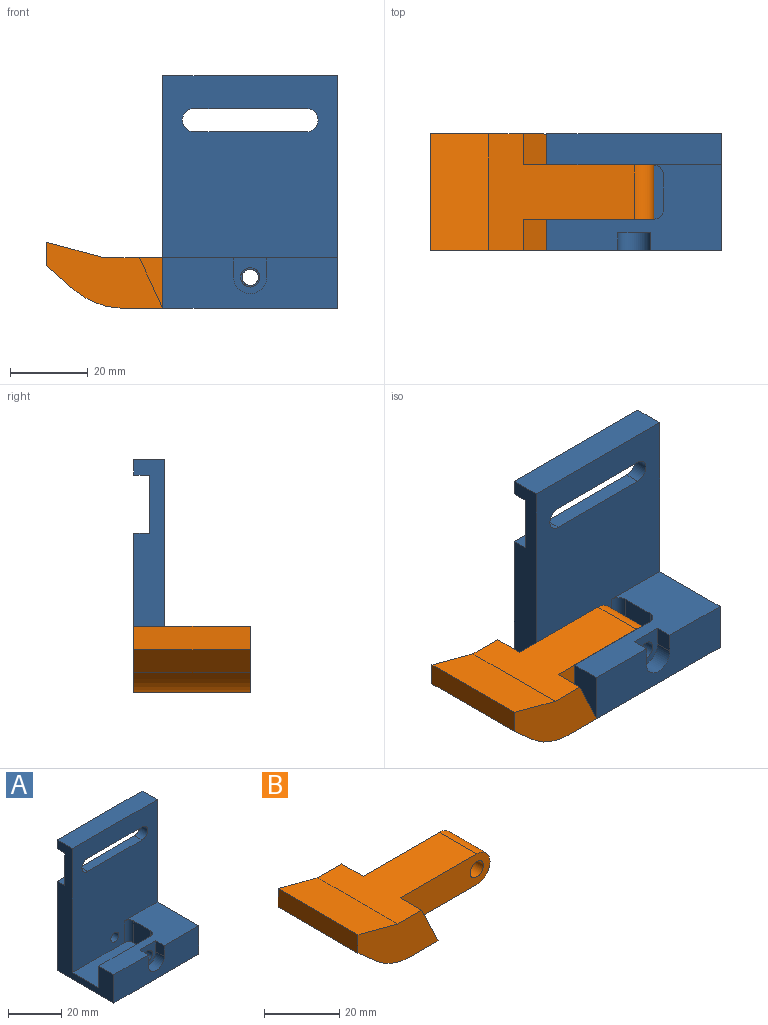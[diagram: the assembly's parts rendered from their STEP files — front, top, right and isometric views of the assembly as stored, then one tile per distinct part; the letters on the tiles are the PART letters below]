
ASSEMBLY  parts=2 mates=1
PART A: 27 faces, bbox 45x30x60 mm
  f0: plane 45x13mm, normal (0,-1,0), area 514.1mm2, adj f2,f5,f6,f8,f24,f25,f26
  f1: cylinder r=2.5mm len=5mm, axis (0,-1,0), area 55mm2, adj f17,f23
  f2: plane 60x30mm, normal (-1,0,0), area 566mm2, adj f0,f3,f4,f5,f7,f8,f9,f10
  f3: plane 45x41mm, normal (0,1,0), area 1831.1mm2, adj f2,f5,f6,f11,f22
  f4: plane 45x8mm, normal (0,0,1), area 360mm2, adj f2,f6,f7,f9
  f5: plane 45x30mm, normal (0,0,-1), area 1350mm2, adj f0,f2,f3,f6
  f6: plane 60x30mm, normal (1,0,0), area 706mm2, adj f0,f3,f4,f5,f7,f8,f9,f10
  f7: plane 45x4mm, normal (0,1,0), area 180mm2, adj f2,f4,f6,f10
  f8: plane 45x22mm, normal (0,0,1), area 534.4mm2, adj f0,f2,f6,f9,f17,f18,f19,f20
  f9: plane 57x45mm, normal (0,-1,0), area 2173.9mm2, adj f2,f4,f6,f8,f13,f14,f15,f16
  f10: plane 45x4mm, normal (0,0,-1), area 180mm2, adj f2,f6,f7,f12
  f11: plane 45x4mm, normal (0,0,1), area 180mm2, adj f2,f3,f6,f12
  f12: plane 45x15mm, normal (0,1,0), area 472.7mm2, adj f2,f6,f10,f11,f13,f14,f15,f16
  f13: plane 29x4mm, normal (0,0,-1), area 116mm2, adj f9,f12,f14,f16
  f14: cylinder r=3mm len=6mm, axis (0,1,0), area 37.7mm2, adj f9,f12,f13,f15
  f15: plane 29x4mm, normal (0,0,1), area 116mm2, adj f9,f12,f14,f16
  f16: cylinder r=3mm len=6mm, axis (0,1,0), area 37.7mm2, adj f9,f12,f13,f15
  f17: plane 27.5x10mm, normal (0,1,0), area 255.4mm2, adj f1,f2,f8,f18,f21
  f18: cylinder r=2.5mm len=10mm, axis (0,0,1), area 39.3mm2, adj f8,f17,f19,f21
  f19: plane 10x9mm, normal (-1,0,0), area 90mm2, adj f8,f18,f20,f21
  f20: cylinder r=2.5mm len=10mm, axis (0,0,1), area 39.3mm2, adj f8,f9,f19,f21
  f21: plane 30x14mm, normal (0,0,1), area 417.3mm2, adj f2,f9,f17,f18,f19,f20
  f22: cylinder r=2.1mm len=8mm, axis (0,1,0), area 105.6mm2, adj f3,f9
  f23: plane 9.25x8.5mm, normal (0,-1,0), area 51.2mm2, adj f1,f8,f24,f25,f26
  f24: plane 5x4.5mm, normal (1,0,0), area 22.5mm2, adj f0,f8,f23,f25
  f25: cylinder r=4.25mm len=8.5mm, axis (0,-1,0), area 60.1mm2, adj f0,f23,f24,f26
  f26: plane 5x4.5mm, normal (-1,0,0), area 22.5mm2, adj f0,f8,f23,f25
PART B: 16 faces, bbox 57.5x30x17 mm
  f0: plane 37.57x30mm, normal (0,0,1), area 670.2mm2, adj f1,f5,f7,f10,f11,f12,f13,f14
  f1: plane 30x17mm, normal (0,1,0), area 305.2mm2, adj f0,f6,f7,f8,f9,f13,f15
  f2: plane 14x3mm, normal (1,0,0), area 42mm2, adj f3,f6,f12,f14
  f3: plane 22.5x14mm, normal (0,0,-1), area 315mm2, adj f2,f5,f12,f14
  f4: cylinder r=2.5mm len=14mm, axis (0,1,0), area 219.9mm2, adj f12,f14
  f5: cylinder r=5mm len=14mm, axis (0,1,0), area 219.9mm2, adj f0,f3,f12,f14
  f6: plane 30x9.97mm, normal (0,0,-1), area 299.1mm2, adj f1,f2,f10,f11,f13,f15
  f7: plane 30x14.93mm, normal (0.26,0,0.97), area 463.6mm2, adj f0,f1,f8,f10
  f8: plane 30x6mm, normal (-1,0,0), area 180mm2, adj f1,f7,f9,f10
  f9: plane 30x6.8mm, normal (-0.66,0,-0.75), area 272.1mm2, adj f1,f8,f10,f15
  f10: plane 30x17mm, normal (0,-1,0), area 305.2mm2, adj f0,f6,f7,f8,f9,f11,f15
  f11: plane 13x8mm, normal (0.91,0,0.42), area 114.8mm2, adj f0,f6,f10,f12
  f12: plane 33.56x13mm, normal (0,-1,0), area 284mm2, adj f0,f2,f3,f4,f5,f11
  f13: plane 13x8mm, normal (0.91,0,0.42), area 114.8mm2, adj f0,f1,f6,f14
  f14: plane 33.56x13mm, normal (0,1,0), area 284mm2, adj f0,f2,f3,f4,f5,f13
  f15: cylinder r=20mm len=30mm, axis (0,-1,0), area 433.7mm2, adj f1,f6,f9,f10
PLACE A t=(-5.42,0.4,2)mm fixed
PLACE B rot(axis=(0,1,0),0deg) t=(-27.93,0.4,2)mm
MATE revolute B.f4 <-> A.f1  axis (0,-1,0) through (-27.92,-21.6,10)mm
